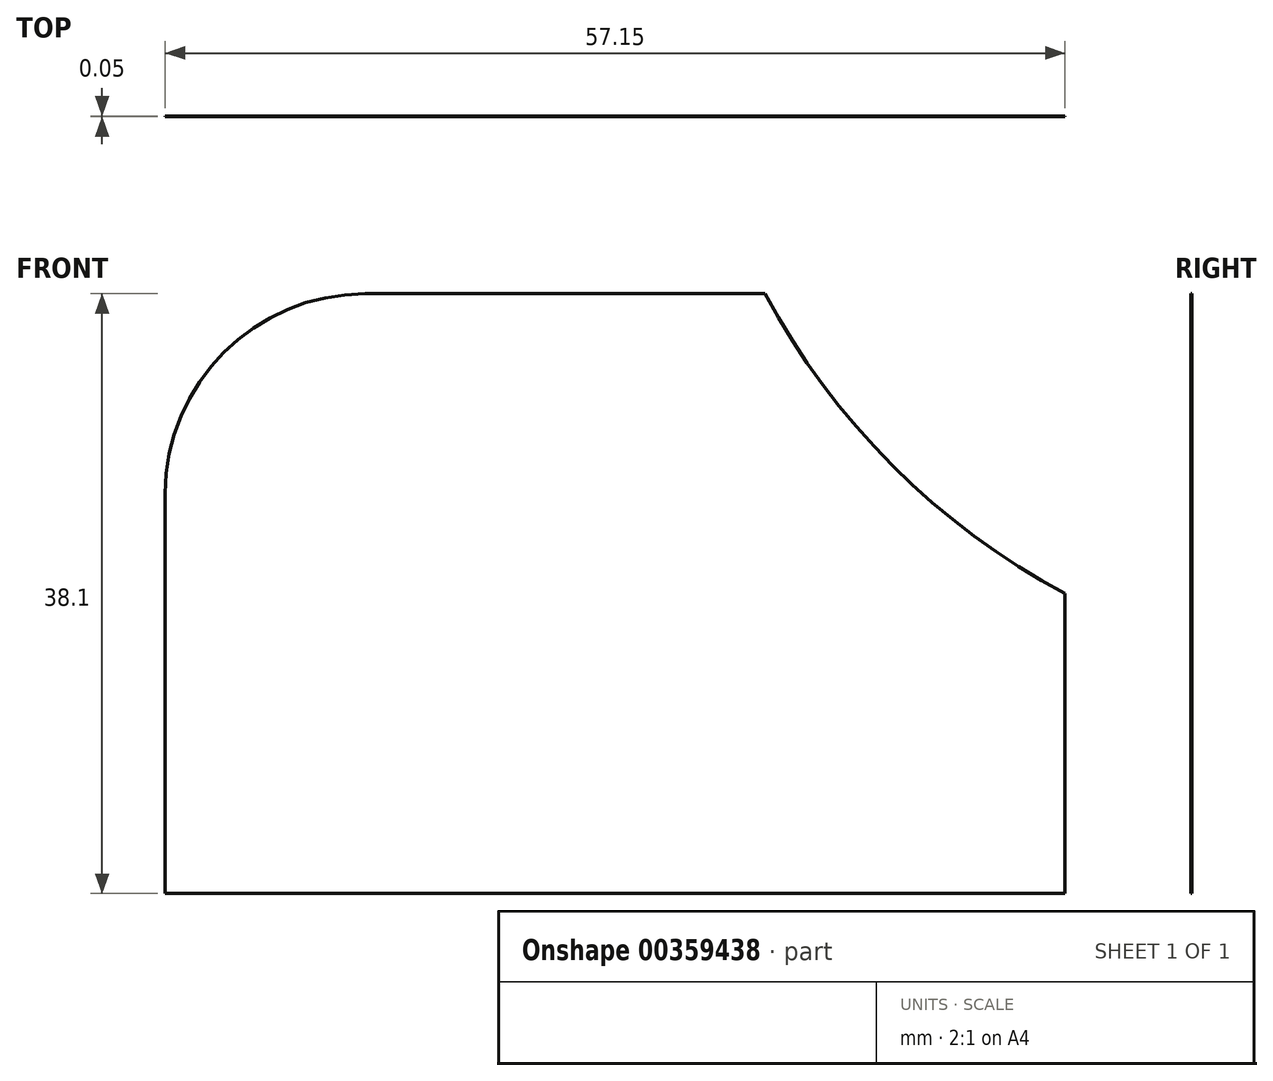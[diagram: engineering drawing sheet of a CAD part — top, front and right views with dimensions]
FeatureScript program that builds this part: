
annotation { "Feature Type Name" : "Feature", "Feature Type Description" : "" }
export const myFeature = defineFeature(function(context is Context, id is Id, definition is map)
    precondition{}
    {
        {
            var Q0;
            Q0=qCreatedBy(makeId("Front.planeOp"),FACE);
            var sketch = newSketch(context, id + "F0", { "sketchPlane" : qUnion([Q0])});
            skLineSegment(sketch, "E0", {"start": v(0, 0) * mm, "end": v(0, 38.1) * mm});
            skLineSegment(sketch, "E1", {"start": v(0, 38.1) * mm, "end": v(57.15, 38.1) * mm});
            skLineSegment(sketch, "E2", {"start": v(57.15, 38.1) * mm, "end": v(57.15, 0) * mm});
            skLineSegment(sketch, "E3", {"start": v(57.15, 0) * mm, "end": v(0, 0) * mm});
            skSolve(sketch);
        }
        {
            var Q0;
            Q0=makeQuery(id+"F0.imprint","IMPRINT",FACE,{"disambiguationData":[TD([[makeQuery(id+"F0.imprint","IMPRINT",EDGE,{"derivedFrom":sQuery(id+"F0.wireOp",EDGE,"E0")}),-1.0]])]});
            extrude(context, id + "F1", {"entities" : qUnion([Q0]), "depth" : 5 / 101.6 * mm});
        }
        {
            var Q0;
            Q0=makeQuery(id+"F1.opExtrude","CAP_FACE",FACE,{"disambiguationData":[OSD([sQuery(id+"F0.wireOp",EDGE,"E0"),sQuery(id+"F0.wireOp",EDGE,"E1"),sQuery(id+"F0.wireOp",EDGE,"E2"),sQuery(id+"F0.wireOp",EDGE,"E3")])],"isStart":false});
            var sketch = newSketch(context, id + "F2", { "sketchPlane" : qUnion([Q0])});
            skArc(sketch, "E4", {"start": v(38.1, 38.1) * mm, "mid": v(46.21, 27.16) * mm, "end": v(57.15, 19.05) * mm});
            skSolve(sketch);
        }
        {
            var Q0;
            Q0 = qSketchRegion(id + "F2", true);
            var Q1;
            {var subQ0=sQuery(id+"F2.wireOp",EDGE,"E4");Q1=makeQuery(id+"F2.imprint","IMPRINT",FACE,{"disambiguationData":[TD([[makeQuery(id+"F2.imprint","IMPRINT",EDGE,{"derivedFrom":subQ0}),1.0]])]});}
            extrude(context, id + "F3", {"entities" : qUnion([Q0, Q1]), "operationType" : NewBodyOperationType.REMOVE, "oppositeDirection" : true, "depth" : 31.75 * mm});
        }
        {
            var Q0;
            Q0=makeQuery(id+"F1.opExtrude","CAP_FACE",FACE,{"disambiguationData":[OSD([sQuery(id+"F0.wireOp",EDGE,"E0"),sQuery(id+"F0.wireOp",EDGE,"E1"),sQuery(id+"F0.wireOp",EDGE,"E2"),sQuery(id+"F0.wireOp",EDGE,"E3")])],"isStart":false});
            var sketch = newSketch(context, id + "F4", { "sketchPlane" : qUnion([Q0])});
            skLineSegment(sketch, "E5", {"start": v(0, 25.4) * mm, "end": v(0, 0) * mm});
            skLineSegment(sketch, "E6", {"start": v(38.1, 38.1) * mm, "end": v(12.7, 38.1) * mm});
            skPoint(sketch, "E7.visualSharp", {"position": v(0, 38.1) * mm});
            skArc(sketch, "E7.filletArc", {"start": v(12.7, 38.1) * mm, "mid": v(3.72, 34.38) * mm, "end": v(0, 25.4) * mm});
            skSolve(sketch);
        }
        {
            var Q0;
            Q0 = qSketchRegion(id + "F4", true);
            var Q1;
            {var subQ0=sQuery(id+"F4.wireOp",EDGE,"FUjHTHJK-ouky-INgD-kWze-lRIxoLMoUMFy");Q1=makeQuery(id+"F4.imprint","IMPRINT",FACE,{"disambiguationData":[TD([[makeQuery(id+"F4.imprint","IMPRINT",EDGE,{"derivedFrom":subQ0}),-1.0]])]});}
            var Q2;
            {var subQ0=sQuery(id+"F4.wireOp",EDGE,"E7.filletArc");Q2=makeQuery(id+"F4.imprint","IMPRINT",FACE,{"disambiguationData":[TD([[makeQuery(id+"F4.imprint","IMPRINT",EDGE,{"derivedFrom":subQ0}),-1.0]])]});}
            extrude(context, id + "F5", {"entities" : qUnion([Q0, Q1, Q2]), "operationType" : NewBodyOperationType.REMOVE, "oppositeDirection" : true, "depth" : 31.75 * mm});
        }
    });
